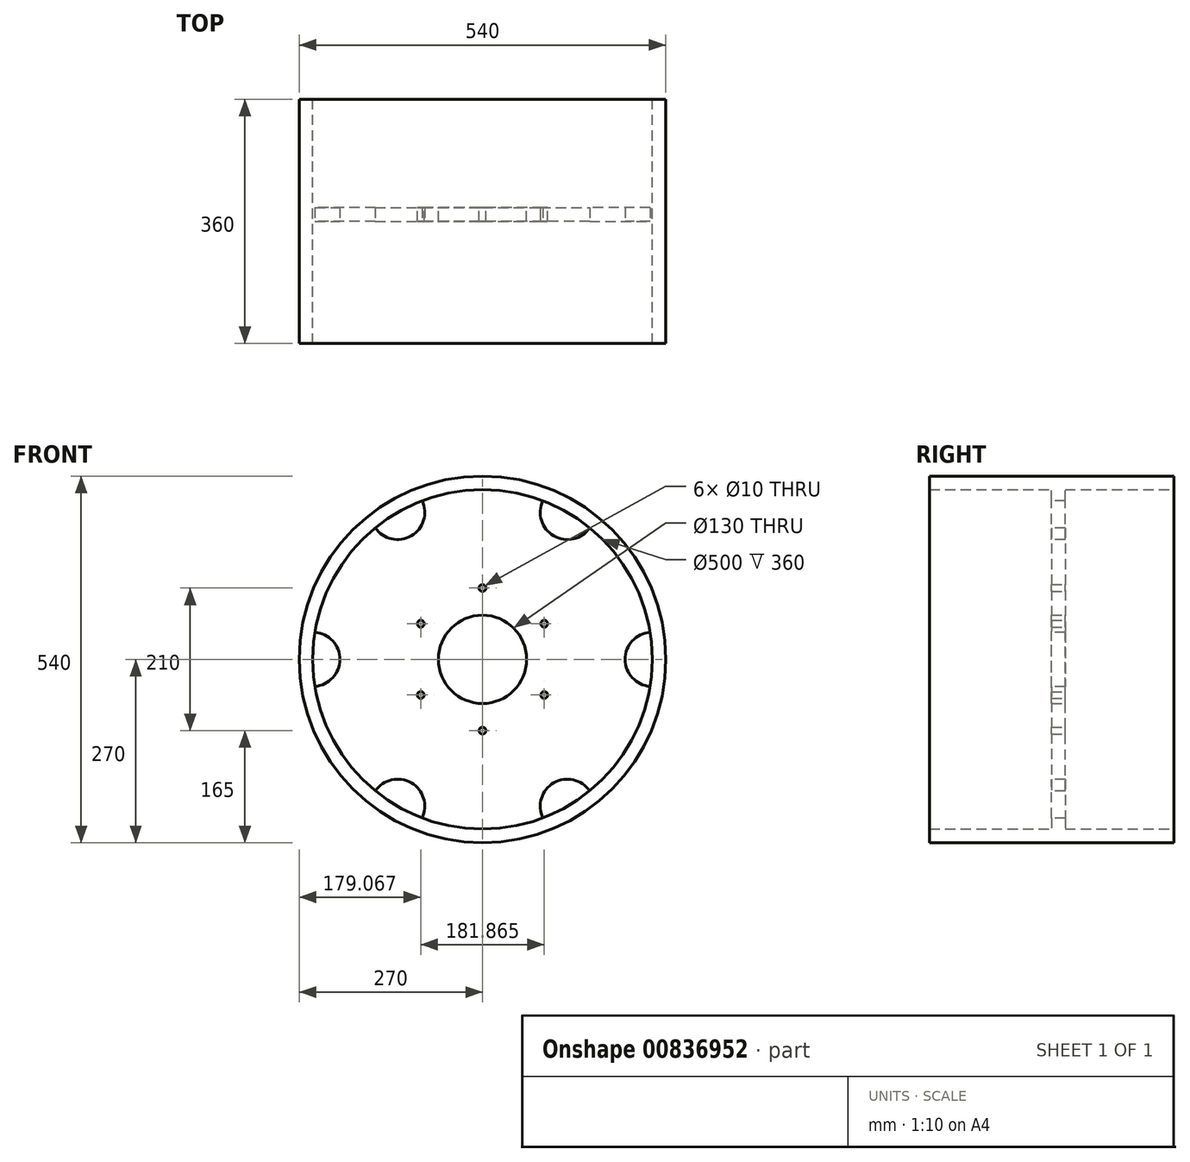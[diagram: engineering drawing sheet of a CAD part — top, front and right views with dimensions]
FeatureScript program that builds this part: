
annotation { "Feature Type Name" : "Feature", "Feature Type Description" : "" }
export const myFeature = defineFeature(function(context is Context, id is Id, definition is map)
    precondition{}
    {
        {
            var Q0;
            Q0=qCreatedBy(makeId("Front.planeOp"),FACE);
            var sketch = newSketch(context, id + "F0", { "sketchPlane" : qUnion([Q0])});
            skCircle(sketch, "E0", {"center": v(0, 0) * mm, "radius": 250 * mm});
            skCircle(sketch, "E1", {"center": v(0, 0) * mm, "radius": 65 * mm});
            skCircle(sketch, "E2", {"center": v(0, 0) * mm, "radius": 105 * mm, "construction": true});
            skLineSegment(sketch, "E3", {"start": v(0, 0) * mm, "end": v(0, 276.05) * mm, "construction": true});
            skLineSegment(sketch, "E4", {"start": v(0, 0) * mm, "end": v(391.8, 0) * mm, "construction": true});
            skCircle(sketch, "E5", {"center": v(0, 105) * mm, "radius": 5 * mm});
            skCircle(sketch, "E6.1.0", {"center": v(-90.93, 52.5) * mm, "radius": 5 * mm});
            skCircle(sketch, "E6.2.0", {"center": v(-90.93, -52.5) * mm, "radius": 5 * mm});
            skCircle(sketch, "E7.1.3.0", {"center": v(0, -105) * mm, "radius": 5 * mm});
            skCircle(sketch, "E7.1.4.0", {"center": v(90.93, -52.5) * mm, "radius": 5 * mm});
            skCircle(sketch, "E7.1.5.0", {"center": v(90.93, 52.5) * mm, "radius": 5 * mm});
            skSolve(sketch);
        }
        {
            var Q0;
            Q0=makeQuery(id+"F0.imprint","IMPRINT",FACE,{"disambiguationData":[TD([[makeQuery(id+"F0.imprint","IMPRINT",EDGE,{"derivedFrom":sQuery(id+"F0.wireOp",EDGE,"E0")}),1.0]])]});
            extrude(context, id + "F1", {"entities" : qUnion([Q0]), "endBound" : BoundingType.SYMMETRIC, "depth" : 20 * mm, "offsetDistance" : 25 * mm});
        }
        {
            var Q0;
            Q0=makeQuery(id+"F1.opExtrude","CAP_FACE",FACE,{"disambiguationData":[OSD([sQuery(id+"F0.wireOp",EDGE,"E0"),sQuery(id+"F0.wireOp",EDGE,"E1"),sQuery(id+"F0.wireOp",EDGE,"E5"),sQuery(id+"F0.wireOp",EDGE,"E6.1.0"),sQuery(id+"F0.wireOp",EDGE,"E6.2.0"),sQuery(id+"F0.wireOp",EDGE,"E7.1.3.0"),sQuery(id+"F0.wireOp",EDGE,"E7.1.4.0"),sQuery(id+"F0.wireOp",EDGE,"E7.1.5.0")])],"isStart":false});
            var sketch = newSketch(context, id + "F2", { "sketchPlane" : qUnion([Q0])});
            skLineSegment(sketch, "E8", {"start": v(0, 0) * mm, "end": v(150.38, 260.47) * mm, "construction": true});
            skArc(sketch, "E9", {"start": v(88.87, 233.67) * mm, "mid": v(105, 181.87) * mm, "end": v(157.93, 193.8) * mm});
            skArc(sketch, "E10.1.0", {"start": v(-157.93, 193.8) * mm, "mid": v(-105, 181.87) * mm, "end": v(-88.87, 233.67) * mm});
            skArc(sketch, "E10.2.0", {"start": v(-246.8, -39.87) * mm, "mid": v(-210, 0) * mm, "end": v(-246.8, 39.87) * mm});
            skArc(sketch, "E10.3.0", {"start": v(-88.87, -233.67) * mm, "mid": v(-105, -181.87) * mm, "end": v(-157.93, -193.8) * mm});
            skArc(sketch, "E10.4.0", {"start": v(157.93, -193.8) * mm, "mid": v(105, -181.87) * mm, "end": v(88.87, -233.67) * mm});
            skArc(sketch, "E10.5.0", {"start": v(246.8, 39.87) * mm, "mid": v(210, 0) * mm, "end": v(246.8, -39.87) * mm});
            skPoint(sketch, "E10.center", {"position": v(0, 0) * mm});
            skSolve(sketch);
        }
        {
            var Q0;
            {var subQ0=sQuery(id+"F2.wireOp",EDGE,"E9");Q0=makeQuery(id+"F2.imprint","IMPRINT",FACE,{"disambiguationData":[TD([[makeQuery(id+"F2.imprint","IMPRINT",EDGE,{"derivedFrom":subQ0}),1.0]])]});}
            var Q1;
            {var subQ0=sQuery(id+"F2.wireOp",EDGE,"E10.5.0");Q1=makeQuery(id+"F2.imprint","IMPRINT",FACE,{"disambiguationData":[TD([[makeQuery(id+"F2.imprint","IMPRINT",EDGE,{"derivedFrom":subQ0}),1.0]])]});}
            var Q2;
            {var subQ0=sQuery(id+"F2.wireOp",EDGE,"E10.4.0");Q2=makeQuery(id+"F2.imprint","IMPRINT",FACE,{"disambiguationData":[TD([[makeQuery(id+"F2.imprint","IMPRINT",EDGE,{"derivedFrom":subQ0}),1.0]])]});}
            var Q3;
            {var subQ0=sQuery(id+"F2.wireOp",EDGE,"E10.3.0");Q3=makeQuery(id+"F2.imprint","IMPRINT",FACE,{"disambiguationData":[TD([[makeQuery(id+"F2.imprint","IMPRINT",EDGE,{"derivedFrom":subQ0}),1.0]])]});}
            var Q4;
            {var subQ0=sQuery(id+"F2.wireOp",EDGE,"E10.2.0");Q4=makeQuery(id+"F2.imprint","IMPRINT",FACE,{"disambiguationData":[TD([[makeQuery(id+"F2.imprint","IMPRINT",EDGE,{"derivedFrom":subQ0}),1.0]])]});}
            var Q5;
            {var subQ0=sQuery(id+"F2.wireOp",EDGE,"E10.1.0");Q5=makeQuery(id+"F2.imprint","IMPRINT",FACE,{"disambiguationData":[TD([[makeQuery(id+"F2.imprint","IMPRINT",EDGE,{"derivedFrom":subQ0}),1.0]])]});}
            extrude(context, id + "F3", {"entities" : qUnion([Q0, Q1, Q2, Q3, Q4, Q5]), "operationType" : NewBodyOperationType.REMOVE, "endBound" : BoundingType.THROUGH_ALL, "oppositeDirection" : true, "depth" : 20 * mm, "offsetDistance" : 25 * mm});
        }
        {
            var Q0;
            Q0=makeQuery(id+"F1.opExtrude","CAP_FACE",FACE,{"disambiguationData":[OSD([sQuery(id+"F0.wireOp",EDGE,"E0"),sQuery(id+"F0.wireOp",EDGE,"E1"),sQuery(id+"F0.wireOp",EDGE,"E5"),sQuery(id+"F0.wireOp",EDGE,"E6.1.0"),sQuery(id+"F0.wireOp",EDGE,"E6.2.0"),sQuery(id+"F0.wireOp",EDGE,"E7.1.3.0"),sQuery(id+"F0.wireOp",EDGE,"E7.1.4.0"),sQuery(id+"F0.wireOp",EDGE,"E7.1.5.0")])],"isStart":false});
            var sketch = newSketch(context, id + "F4", { "sketchPlane" : qUnion([Q0])});
            skCircle(sketch, "E11", {"center": v(0, 0) * mm, "radius": 270 * mm});
            skCircle(sketch, "E12", {"center": v(0, 0) * mm, "radius": 250 * mm});
            skSolve(sketch);
        }
        {
            var Q0;
            Q0=makeQuery(id+"F4.imprint","IMPRINT",FACE,{"disambiguationData":[TD([[makeQuery(id+"F4.imprint","IMPRINT",EDGE,{"derivedFrom":sQuery(id+"F4.wireOp",EDGE,"E11")}),1.0]])]});
            extrude(context, id + "F5", {"entities" : qUnion([Q0]), "operationType" : NewBodyOperationType.ADD, "endBound" : BoundingType.SYMMETRIC, "depth" : 360 * mm, "offsetDistance" : 25 * mm});
        }
    });
